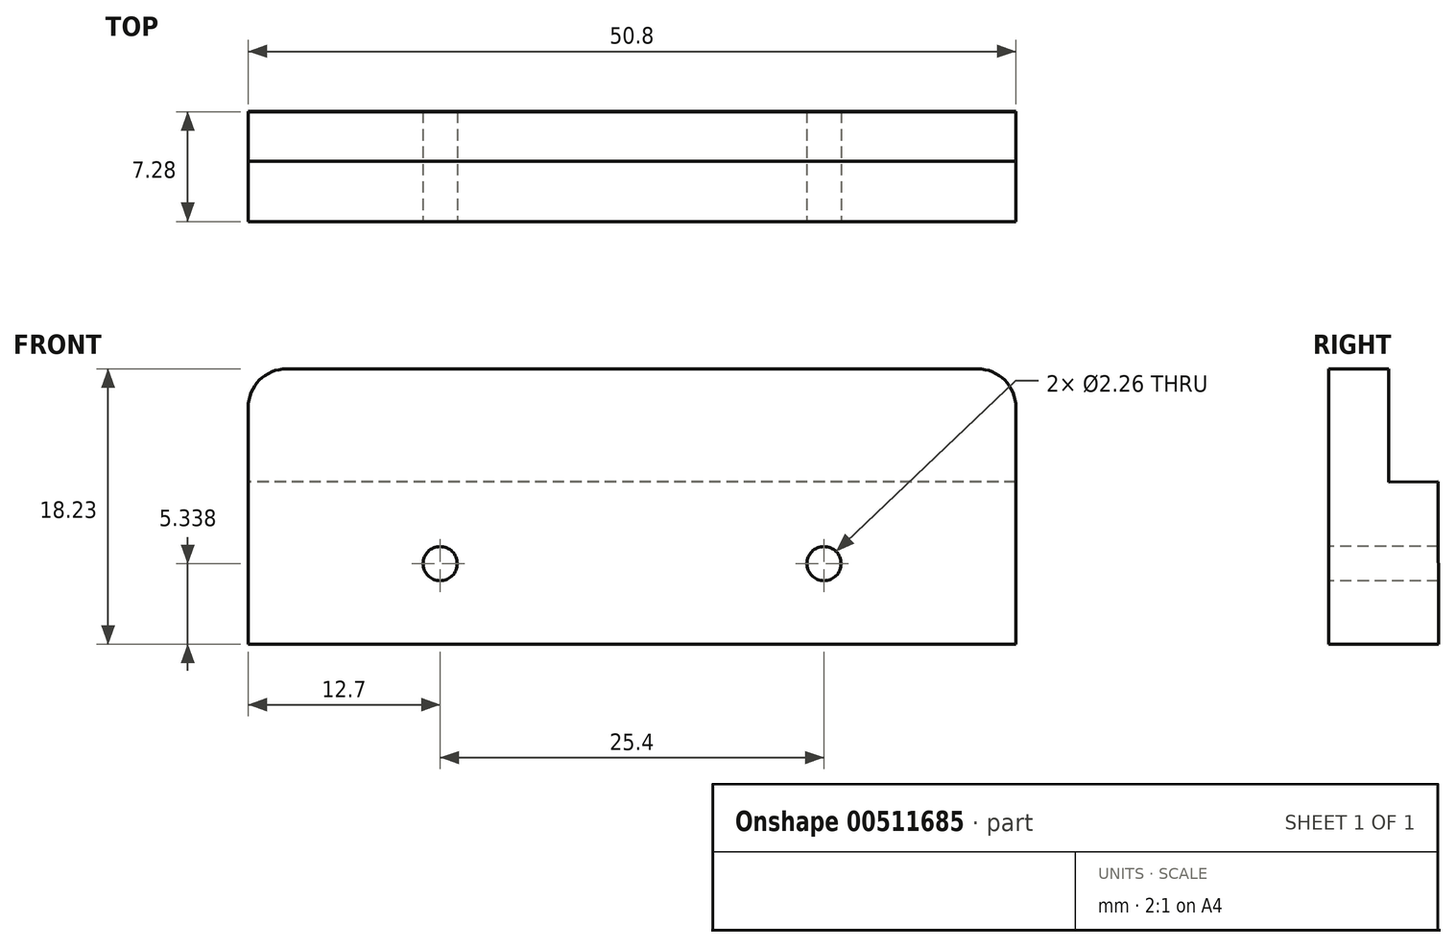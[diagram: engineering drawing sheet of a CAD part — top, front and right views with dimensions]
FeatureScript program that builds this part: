
annotation { "Feature Type Name" : "Feature", "Feature Type Description" : "" }
export const myFeature = defineFeature(function(context is Context, id is Id, definition is map)
    precondition{}
    {
        {
            var Q0;
            Q0=qCreatedBy(makeId("Right.planeOp"),FACE);
            var sketch = newSketch(context, id + "F0", { "sketchPlane" : qUnion([Q0])});
            skLineSegment(sketch, "E0", {"start": v(-2.3, 7.17) * mm, "end": v(-2.3, -0.33) * mm});
            skLineSegment(sketch, "E1", {"start": v(-2.3, -0.33) * mm, "end": v(0.94, -0.3) * mm});
            skLineSegment(sketch, "E2", {"start": v(-6.3, 7.17) * mm, "end": v(-2.3, 7.17) * mm});
            skLineSegment(sketch, "E3", {"start": v(-6.3, 7.17) * mm, "end": v(-6.3, -11.06) * mm});
            skLineSegment(sketch, "E4", {"start": v(-6.3, -11.06) * mm, "end": v(0.97, -11.06) * mm});
            skLineSegment(sketch, "E5", {"start": v(0.94, -0.3) * mm, "end": v(0.97, -11.06) * mm});
            skSolve(sketch);
        }
        {
            var Q0;
            Q0=makeQuery(id+"F0.imprint","IMPRINT",FACE,{"disambiguationData":[TD([[makeQuery(id+"F0.imprint","IMPRINT",EDGE,{"derivedFrom":sQuery(id+"F0.wireOp",EDGE,"E0")}),-1.0]])]});
            extrude(context, id + "F1", {"entities" : qUnion([Q0]), "depth" : 50.8 * mm, "offsetDistance" : 25.4 * mm});
        }
        {
            var Q0;
            Q0=makeQuery(id+"F1.opExtrude","SWEPT_FACE",FACE,{"disambiguationData":[OSD([sQuery(id+"F0.wireOp",EDGE,"E3")])]});
            var sketch = newSketch(context, id + "F2", { "sketchPlane" : qUnion([Q0])});
            skPoint(sketch, "E6", {"position": v(12.7, -5.72) * mm});
            skPoint(sketch, "E7", {"position": v(38.1, -5.72) * mm});
            skSolve(sketch);
        }
        {
            var Q0;
            Q0=sQuery(id+"F2.wireOp",VERTEX,"E6");
            var Q1;
            Q1=sQuery(id+"F2.wireOp",VERTEX,"E7");
            var Q2;
            Q2=makeQuery(id+"F1.opExtrude","SWEPT_BODY",BODY,{"disambiguationData":[OSD([sQuery(id+"F0.wireOp",EDGE,"E0"),sQuery(id+"F0.wireOp",EDGE,"E1"),sQuery(id+"F0.wireOp",EDGE,"E2"),sQuery(id+"F0.wireOp",EDGE,"E3"),sQuery(id+"F0.wireOp",EDGE,"E4"),sQuery(id+"F0.wireOp",EDGE,"E5")])]});
            hole(context, id + "F3", {"style" : HoleStyle.SIMPLE, "endStyle" : HoleEndStyle.THROUGH, "standardTappedOrClearance" : lookupTablePath({ "standard" : "ANSI", "engagement" : "75%", "pitch" : "40 tpi", "size" : "#4", "type" : "Tapped" }), "standardBlindInLast" : lookupTablePath({ "standard" : "ANSI", "engagement" : "75%", "pitch" : "40 tpi", "size" : "#4", "type" : "Tapped" }), "holeDiameter" : 2.26 * mm, "showTappedDepth" : true, "isTappedThrough" : true, "tappedDepth" : 12.7 * mm, "tapClearance" : 3, "locations" : qUnion([Q0, Q1]), "scope" : qUnion([Q2]), "majorDiameter" : 2.84 * mm});
        }
        {
            var Q0;
            Q0=makeQuery(id+"F1.opExtrude","CAP_EDGE",EDGE,{"disambiguationData":[OSD([sQuery(id+"F0.wireOp",EDGE,"E2")])],"isStart":false});
            fillet(context, id + "F4", {"entities" : qUnion([Q0]), "radius" : 2.54 * mm, "tangentPropagation" : true, "allowEdgeOverflow" : false});
        }
        {
            var Q0;
            Q0=makeQuery(id+"F1.opExtrude","CAP_EDGE",EDGE,{"disambiguationData":[OSD([sQuery(id+"F0.wireOp",EDGE,"E2")])],"isStart":true});
            fillet(context, id + "F5", {"entities" : qUnion([Q0]), "radius" : 2.54 * mm, "tangentPropagation" : true, "allowEdgeOverflow" : false});
        }
    });
